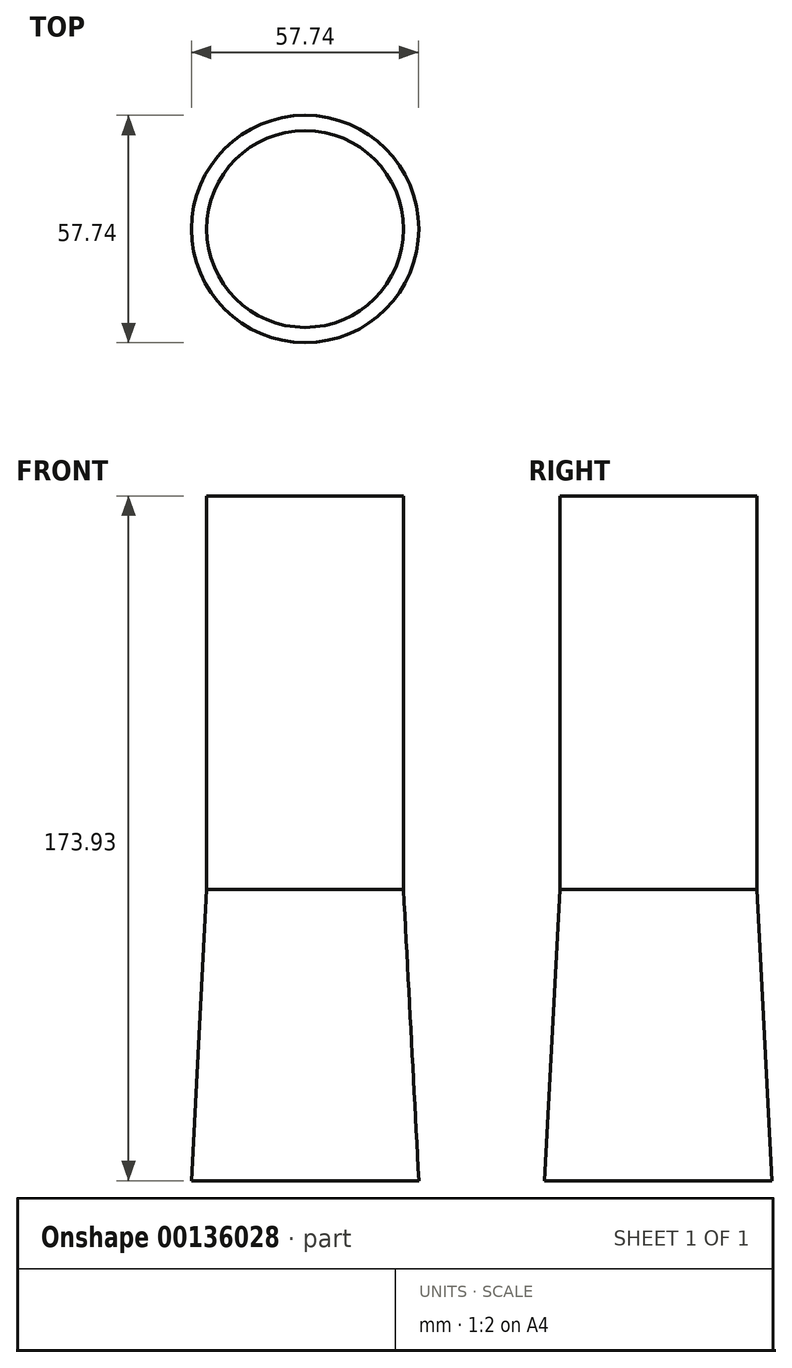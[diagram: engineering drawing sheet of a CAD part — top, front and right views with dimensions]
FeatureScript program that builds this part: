
annotation { "Feature Type Name" : "Feature", "Feature Type Description" : "" }
export const myFeature = defineFeature(function(context is Context, id is Id, definition is map)
    precondition{}
    {
        {
            var Q0;
            Q0=qCreatedBy(makeId("Top.planeOp"),FACE);
            var sketch = newSketch(context, id + "F0", { "sketchPlane" : qUnion([Q0])});
            skCircle(sketch, "E0", {"center": v(0, 0) * mm, "radius": 25 * mm});
            skSolve(sketch);
        }
        {
            var Q0;
            Q0 = qSketchRegion(id + "F0", true);
            extrude(context, id + "F1", {"entities" : qUnion([Q0]), "depth" : 100 * mm, "hasSecondDirection" : true, "secondDirectionOppositeDirection" : true, "secondDirectionDepth" : 73.93 * mm, "hasSecondDirectionDraft" : true, "secondDirectionDraftAngle" : 3 * degree});
        }
    });
